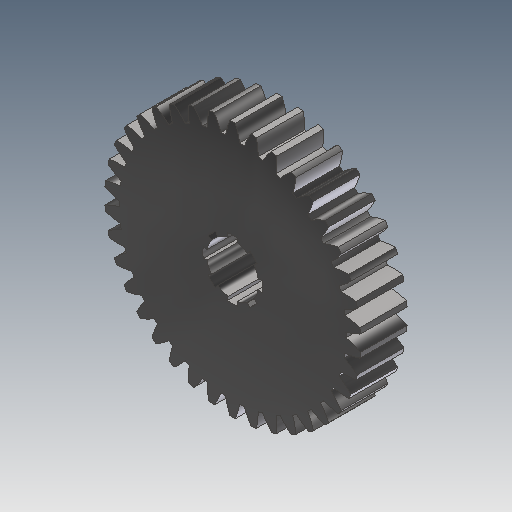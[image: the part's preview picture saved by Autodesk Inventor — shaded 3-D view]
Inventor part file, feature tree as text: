
AUTODESK INVENTOR PART (.ipt)
format: ipt  version: 2017 (Build 210142000, 142)  size: 358,400 bytes
history: native  units: mm (DEFAULTED — no unit token found)
features: sketch x4, extrude x3, plane x3, other x3, pattern_circular x1
ambient origin geometry x8: Origin, YZ Plane, XZ Plane, XY Plane, X Axis, Y Axis, Z Axis, Center Point
bodies: Solid1 (feature_tree)
feature tree (14):
  extrude  "Extrusion1"  Depth=1.8mm TaperAngle=0.0deg
  plane  "Work Plane2"
  plane  "Work Plane8"
  plane  "Work Plane9"
  other  "Цилиндрическое зубчатое зацепление"
  extrude  "Выдавливание2"  Depth=10.0mm TaperAngle=0.0deg
  extrude  "Выдавливание3"  Depth=1.8mm
  pattern_circular  "Круговой массив1"  [2 undecoded]
  sketch  "Sketch1"  dims[d0=9.865mm d1=1.8mm d2=0.0mm]
  sketch  "Sketch2"  dims[d3=9.5mm d4=10.0mm d5=0.0mm d16=6.0mm d17=0.0mm d34=0.826735mm d39=0.0mm d41=0.0mm d43=6.0mm d46=6.0mm d47=0.0mm d48=0.0mm d49=2.0mm d50=10.0mm d51=0.0mm d53=2.3mm d54=3.490659mm d55=1.8mm d56=0.0mm d57=80.0mm d58=360.0deg]
  other  "Srf1"
  sketch  "Эскиз3"
  sketch  "Эскиз4"
  other  "Средний диаметр"
note: 2 required parameter values undecoded (feature->parameter linkage not recoverable at this tier; creation-order binding heuristic only, values carry confidence <= 0.55)
